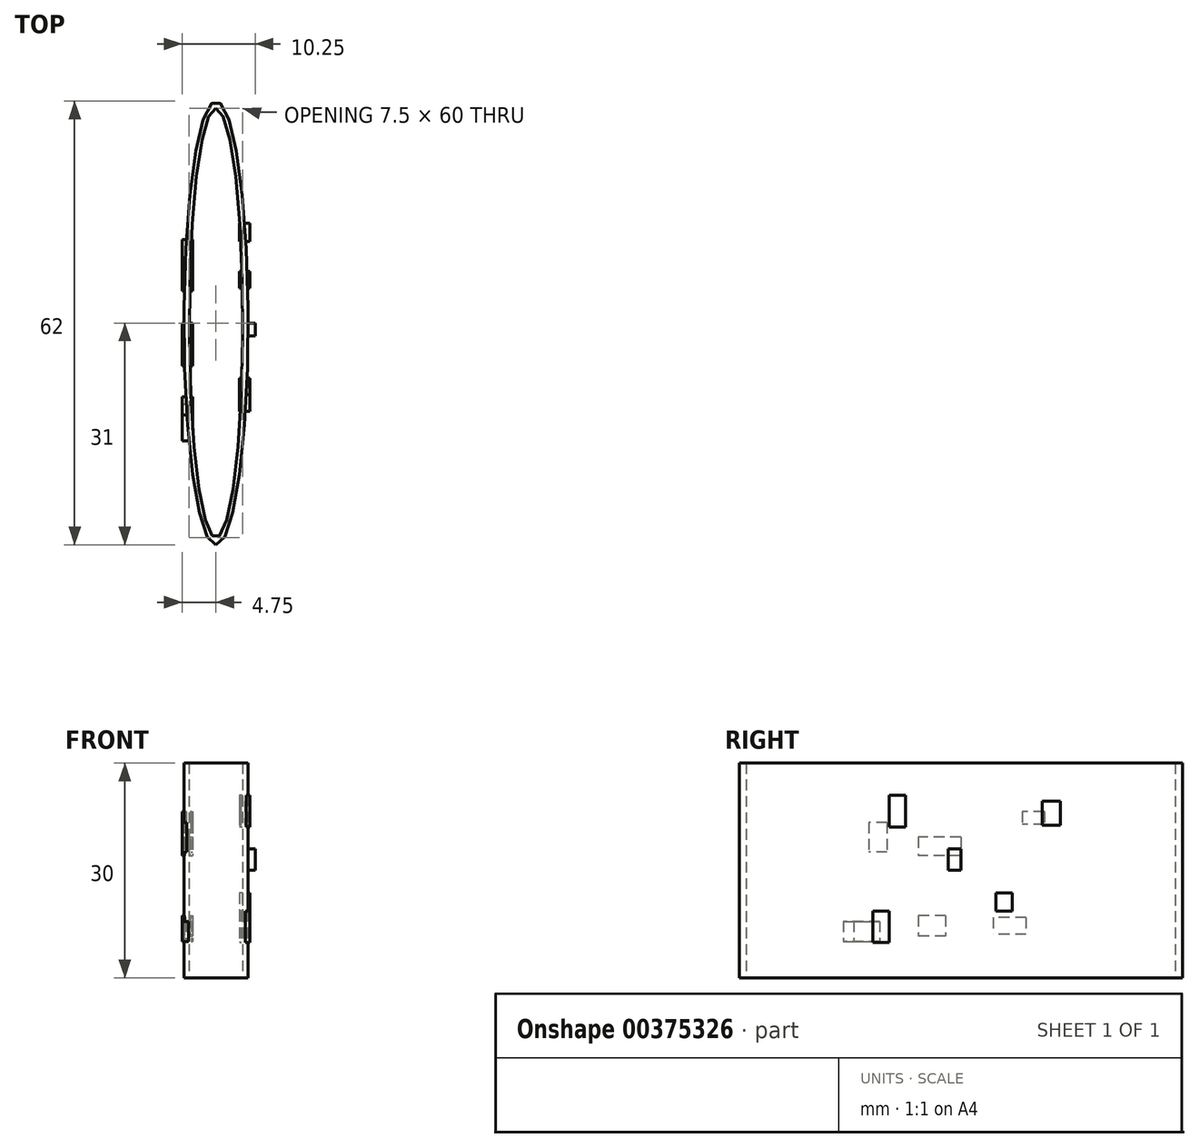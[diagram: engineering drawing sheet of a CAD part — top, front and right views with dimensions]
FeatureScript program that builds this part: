
annotation { "Feature Type Name" : "Feature", "Feature Type Description" : "" }
export const myFeature = defineFeature(function(context is Context, id is Id, definition is map)
    precondition{}
    {
        {
            var Q0;
            Q0=qCreatedBy(makeId("Top.planeOp"),FACE);
            var sketch = newSketch(context, id + "F0", { "sketchPlane" : qUnion([Q0])});
            skEllipse(sketch, "E0", {"center": v(0, 0) * mm, "majorRadius": 30 * mm, "minorRadius": 3.75 * mm, "majorAxis": v(0, 1)});
            skEllipse(sketch, "E1", {"center": v(0, 0) * mm, "majorRadius": 31 * mm, "minorRadius": 4.5 * mm, "majorAxis": v(0, -1)});
            skSolve(sketch);
        }
        {
            var Q0;
            Q0=makeQuery(id+"F0.imprint","IMPRINT",FACE,{"disambiguationData":[TD([[makeQuery(id+"F0.imprint","IMPRINT",EDGE,{"derivedFrom":sQuery(id+"F0.wireOp",EDGE,"E0")}),-1.0]])]});
            extrude(context, id + "F1", {"entities" : qUnion([Q0]), "endBound" : BoundingType.SYMMETRIC, "depth" : 30 * mm});
        }
        {
            var Q0;
            Q0=qCreatedBy(makeId("Right.planeOp"),FACE);
            var Q1;
            Q1 = qBodyType(qCreatedBy(id + "F8" ,EDGE), BodyType.WIRE);
            cPlane(context, id + "F2", {"entities" : qUnion([Q0, Q1]), "cplaneType" : CPlaneType.OFFSET, "offset" : 4 * mm, "width" : 150 * mm, "height" : 150 * mm});
        }
        {
            var Q0;
            Q0=qCreatedBy(id+"F2.planeOp",FACE);
            var sketch = newSketch(context, id + "F3", { "sketchPlane" : qUnion([Q0])});
            skLineSegment(sketch, "E2.bottom", {"start": v(-1.77, 3.02) * mm, "end": v(0, 3.02) * mm});
            skLineSegment(sketch, "E2.top", {"start": v(-1.77, 0) * mm, "end": v(0, 0) * mm});
            skLineSegment(sketch, "E2.left", {"start": v(-1.77, 3.02) * mm, "end": v(-1.77, 0) * mm});
            skLineSegment(sketch, "E2.right", {"start": v(0, 3.02) * mm, "end": v(0, 0) * mm});
            skSolve(sketch);
        }
        {
            var Q0;
            Q0=makeQuery(id+"F3.imprint","IMPRINT",FACE,{"disambiguationData":[TD([[makeQuery(id+"F3.imprint","IMPRINT",EDGE,{"derivedFrom":sQuery(id+"F3.wireOp",EDGE,"E2.bottom")}),-1.0]])]});
            extrude(context, id + "F4", {"entities" : qUnion([Q0]), "operationType" : NewBodyOperationType.ADD, "depth" : 1.5 * mm});
        }
        {
            var Q0;
            Q0=qCreatedBy(id+"F2.planeOp",FACE);
            var sketch = newSketch(context, id + "F5", { "sketchPlane" : qUnion([Q0])});
            skLineSegment(sketch, "E3.bottom", {"start": v(4.9, -3.16) * mm, "end": v(7.2, -3.16) * mm});
            skLineSegment(sketch, "E3.top", {"start": v(4.9, -5.68) * mm, "end": v(7.2, -5.68) * mm});
            skLineSegment(sketch, "E3.left", {"start": v(4.9, -3.16) * mm, "end": v(4.9, -5.68) * mm});
            skLineSegment(sketch, "E3.right", {"start": v(7.2, -3.16) * mm, "end": v(7.2, -5.68) * mm});
            skLineSegment(sketch, "E4.bottom", {"start": v(-12.32, -5.68) * mm, "end": v(-10.01, -5.68) * mm});
            skLineSegment(sketch, "E4.top", {"start": v(-12.32, -10.09) * mm, "end": v(-10.01, -10.09) * mm});
            skLineSegment(sketch, "E4.left", {"start": v(-12.32, -5.68) * mm, "end": v(-12.32, -10.09) * mm});
            skLineSegment(sketch, "E4.right", {"start": v(-10.01, -5.68) * mm, "end": v(-10.01, -10.09) * mm});
            skLineSegment(sketch, "E5.bottom", {"start": v(-10.01, 10.5) * mm, "end": v(-7.7, 10.5) * mm});
            skLineSegment(sketch, "E5.top", {"start": v(-10.01, 6.09) * mm, "end": v(-7.7, 6.09) * mm});
            skLineSegment(sketch, "E5.left", {"start": v(-10.01, 10.5) * mm, "end": v(-10.01, 6.09) * mm});
            skLineSegment(sketch, "E5.right", {"start": v(-7.7, 10.5) * mm, "end": v(-7.7, 6.09) * mm});
            skLineSegment(sketch, "E6.bottom", {"start": v(11.41, 9.66) * mm, "end": v(13.93, 9.66) * mm});
            skLineSegment(sketch, "E6.top", {"start": v(11.41, 6.3) * mm, "end": v(13.93, 6.3) * mm});
            skLineSegment(sketch, "E6.left", {"start": v(11.41, 9.66) * mm, "end": v(11.41, 6.3) * mm});
            skLineSegment(sketch, "E6.right", {"start": v(13.93, 9.66) * mm, "end": v(13.93, 6.3) * mm});
            skSolve(sketch);
        }
        {
            var Q0;
            Q0 = qSketchRegion(id + "F5", true);
            extrude(context, id + "F6", {"entities" : qUnion([Q0]), "operationType" : NewBodyOperationType.ADD, "endBound" : BoundingType.SYMMETRIC, "depth" : 1.5 * mm});
        }
        {
            var Q0;
            Q0=qCreatedBy(makeId("Right.planeOp"),FACE);
            cPlane(context, id + "F7", {"entities" : qUnion([Q0]), "cplaneType" : CPlaneType.OFFSET, "offset" : 4 * mm, "oppositeDirection" : true, "width" : 150 * mm, "height" : 150 * mm});
        }
        {
            var Q0;
            Q0=qCreatedBy(id+"F7.planeOp",FACE);
            var sketch = newSketch(context, id + "F8", { "sketchPlane" : qUnion([Q0])});
            skLineSegment(sketch, "E7.bottom", {"start": v(11.67, 8.22) * mm, "end": v(8.6, 8.22) * mm});
            skLineSegment(sketch, "E7.top", {"start": v(11.67, 6.43) * mm, "end": v(8.6, 6.43) * mm});
            skLineSegment(sketch, "E7.left", {"start": v(11.67, 8.22) * mm, "end": v(11.67, 6.43) * mm});
            skLineSegment(sketch, "E7.right", {"start": v(8.6, 8.22) * mm, "end": v(8.6, 6.43) * mm});
            skLineSegment(sketch, "E8.bottom", {"start": v(-10.32, 6.68) * mm, "end": v(-12.87, 6.68) * mm});
            skLineSegment(sketch, "E8.top", {"start": v(-10.32, 2.6) * mm, "end": v(-12.87, 2.6) * mm});
            skLineSegment(sketch, "E8.left", {"start": v(-10.32, 6.68) * mm, "end": v(-10.32, 2.6) * mm});
            skLineSegment(sketch, "E8.right", {"start": v(-12.87, 6.68) * mm, "end": v(-12.87, 2.6) * mm});
            skLineSegment(sketch, "E9.bottom", {"start": v(-16.45, -7.12) * mm, "end": v(-11.34, -7.12) * mm});
            skLineSegment(sketch, "E9.top", {"start": v(-16.45, -9.93) * mm, "end": v(-11.34, -9.93) * mm});
            skLineSegment(sketch, "E9.left", {"start": v(-16.45, -7.12) * mm, "end": v(-16.45, -9.93) * mm});
            skLineSegment(sketch, "E9.right", {"start": v(-11.34, -7.12) * mm, "end": v(-11.34, -9.93) * mm});
            skLineSegment(sketch, "E10.bottom", {"start": v(9.11, -6.6) * mm, "end": v(4.51, -6.6) * mm});
            skLineSegment(sketch, "E10.top", {"start": v(9.11, -8.9) * mm, "end": v(4.51, -8.9) * mm});
            skLineSegment(sketch, "E10.left", {"start": v(9.11, -6.6) * mm, "end": v(9.11, -8.9) * mm});
            skLineSegment(sketch, "E10.right", {"start": v(4.51, -6.6) * mm, "end": v(4.51, -8.9) * mm});
            skLineSegment(sketch, "E11.bottom", {"start": v(0, 4.64) * mm, "end": v(-5.97, 4.64) * mm});
            skLineSegment(sketch, "E11.top", {"start": v(0, 2.08) * mm, "end": v(-5.97, 2.08) * mm});
            skLineSegment(sketch, "E11.left", {"start": v(0, 4.64) * mm, "end": v(0, 2.08) * mm});
            skLineSegment(sketch, "E11.right", {"start": v(-5.97, 4.64) * mm, "end": v(-5.97, 2.08) * mm});
            skLineSegment(sketch, "E12.bottom", {"start": v(-2.14, -6.35) * mm, "end": v(-5.97, -6.35) * mm});
            skLineSegment(sketch, "E12.top", {"start": v(-2.14, -9.16) * mm, "end": v(-5.97, -9.16) * mm});
            skLineSegment(sketch, "E12.left", {"start": v(-2.14, -6.35) * mm, "end": v(-2.14, -9.16) * mm});
            skLineSegment(sketch, "E12.right", {"start": v(-5.97, -6.35) * mm, "end": v(-5.97, -9.16) * mm});
            skSolve(sketch);
        }
        {
            var Q0;
            Q0 = qSketchRegion(id + "F8", true);
            extrude(context, id + "F9", {"entities" : qUnion([Q0]), "operationType" : NewBodyOperationType.ADD, "endBound" : BoundingType.SYMMETRIC, "oppositeDirection" : true, "depth" : 1.5 * mm});
        }
    });
